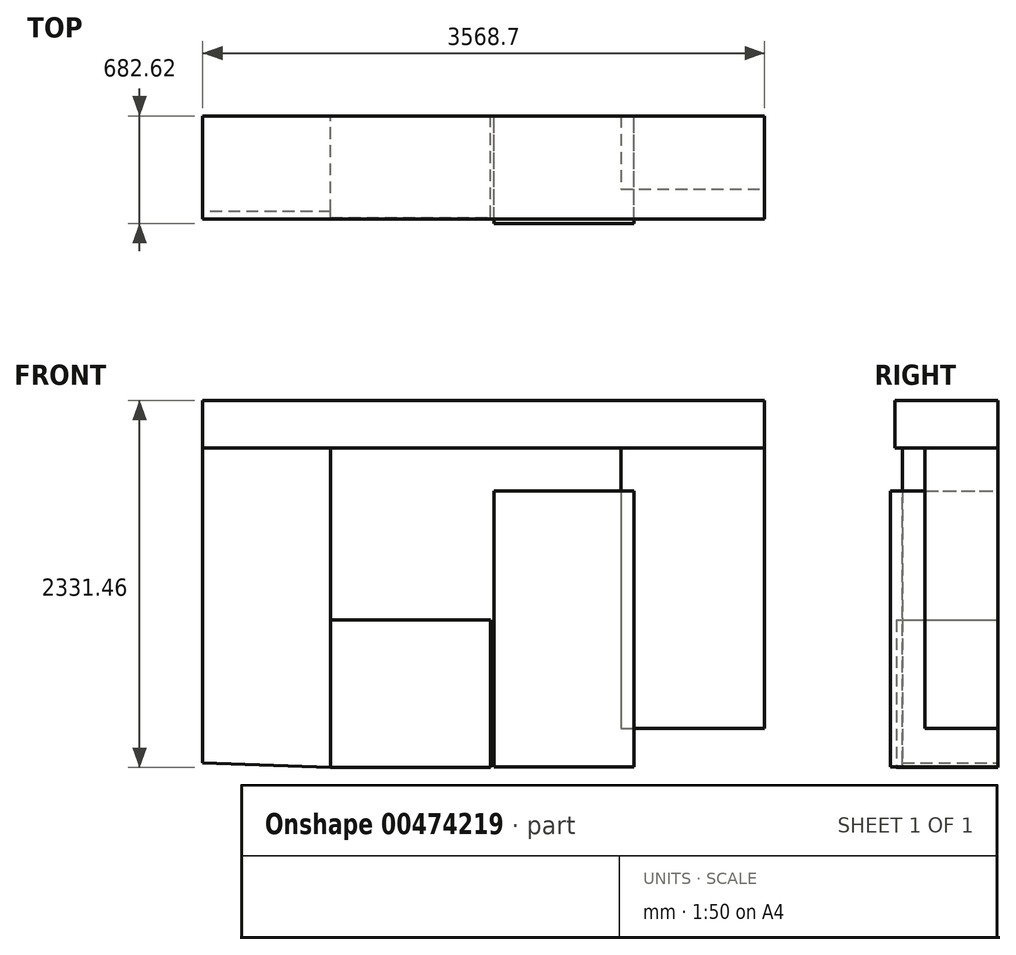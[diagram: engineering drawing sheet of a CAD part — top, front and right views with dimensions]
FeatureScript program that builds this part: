
annotation { "Feature Type Name" : "Feature", "Feature Type Description" : "" }
export const myFeature = defineFeature(function(context is Context, id is Id, definition is map)
    precondition{}
    {
        {
            var Q0;
            Q0=qCreatedBy(makeId("Front.planeOp"),FACE);
            var sketch = newSketch(context, id + "F0", { "sketchPlane" : qUnion([Q0])});
            skLineSegment(sketch, "E0", {"start": v(-765.79, -907.19) * mm, "end": v(-765.79, 1093.06) * mm});
            skLineSegment(sketch, "E1", {"start": v(-765.79, 1093.06) * mm, "end": v(47.01, 1093.06) * mm});
            skLineSegment(sketch, "E2", {"start": v(47.01, 1093.06) * mm, "end": v(47.01, -936.77) * mm});
            skLineSegment(sketch, "E3", {"start": v(47.01, -936.77) * mm, "end": v(-765.79, -907.19) * mm});
            skSolve(sketch);
        }
        {
            var Q0;
            Q0 = qSketchRegion(id + "F0", true);
            extrude(context, id + "F1", {"entities" : qUnion([Q0]), "depth" : 606.42 * mm});
        }
        {
            var Q0;
            Q0=makeQuery(id+"F1.opExtrude","CAP_FACE",FACE,{"disambiguationData":[OSD([sQuery(id+"F0.wireOp",EDGE,"E0"),sQuery(id+"F0.wireOp",EDGE,"E1"),sQuery(id+"F0.wireOp",EDGE,"E2"),sQuery(id+"F0.wireOp",EDGE,"E3")])],"isStart":false});
            var sketch = newSketch(context, id + "F2", { "sketchPlane" : qUnion([Q0])});
            skLineSegment(sketch, "E4", {"start": v(47.01, 0) * mm, "end": v(1063.01, 0) * mm});
            skLineSegment(sketch, "E5", {"start": v(1063.01, 0) * mm, "end": v(1063.01, -936.77) * mm});
            skLineSegment(sketch, "E6", {"start": v(1063.01, -936.77) * mm, "end": v(47.01, -936.77) * mm});
            skLineSegment(sketch, "E7", {"start": v(47.01, -936.77) * mm, "end": v(47.01, 0) * mm});
            skSolve(sketch);
        }
        {
            var Q0;
            Q0 = qSketchRegion(id + "F2", true);
            extrude(context, id + "F3", {"entities" : qUnion([Q0]), "operationType" : NewBodyOperationType.ADD, "depth" : 38.1 * mm, "hasSecondDirection" : true, "secondDirectionOppositeDirection" : true, "secondDirectionDepth" : 606.42 * mm});
        }
        {
            var Q0;
            Q0=makeQuery(id+"F1.opExtrude","CAP_FACE",FACE,{"disambiguationData":[OSD([sQuery(id+"F0.wireOp",EDGE,"E0"),sQuery(id+"F0.wireOp",EDGE,"E1"),sQuery(id+"F0.wireOp",EDGE,"E2"),sQuery(id+"F0.wireOp",EDGE,"E3")])],"isStart":false});
            var sketch = newSketch(context, id + "F4", { "sketchPlane" : qUnion([Q0])});
            skLineSegment(sketch, "E8.bottom", {"start": v(-765.79, 1093.06) * mm, "end": v(2802.91, 1093.06) * mm});
            skLineSegment(sketch, "E8.top", {"start": v(-765.79, 1394.69) * mm, "end": v(2802.91, 1394.69) * mm});
            skLineSegment(sketch, "E8.left", {"start": v(-765.79, 1093.06) * mm, "end": v(-765.79, 1394.69) * mm});
            skLineSegment(sketch, "E8.right", {"start": v(2802.91, 1093.06) * mm, "end": v(2802.91, 1394.69) * mm});
            skSolve(sketch);
        }
        {
            var Q0;
            Q0 = qSketchRegion(id + "F4", true);
            extrude(context, id + "F5", {"entities" : qUnion([Q0]), "operationType" : NewBodyOperationType.ADD, "oppositeDirection" : true, "depth" : 606.42 * mm, "hasSecondDirection" : true, "secondDirectionOppositeDirection" : false, "secondDirectionDepth" : 47.62 * mm});
        }
        {
            var Q0;
            Q0=makeQuery(id+"F1.opExtrude","CAP_FACE",FACE,{"disambiguationData":[OSD([sQuery(id+"F0.wireOp",EDGE,"E0"),sQuery(id+"F0.wireOp",EDGE,"E1"),sQuery(id+"F0.wireOp",EDGE,"E2"),sQuery(id+"F0.wireOp",EDGE,"E3")])],"isStart":false});
            var sketch = newSketch(context, id + "F6", { "sketchPlane" : qUnion([Q0])});
            skLineSegment(sketch, "E9.bottom", {"start": v(1084.55, -933.9) * mm, "end": v(1973.55, -933.9) * mm});
            skLineSegment(sketch, "E9.top", {"start": v(1084.55, 818.7) * mm, "end": v(1973.55, 818.7) * mm});
            skLineSegment(sketch, "E9.left", {"start": v(1084.55, -933.9) * mm, "end": v(1084.55, 818.7) * mm});
            skLineSegment(sketch, "E9.right", {"start": v(1973.55, -933.9) * mm, "end": v(1973.55, 818.7) * mm});
            skSolve(sketch);
        }
        {
            var Q0;
            Q0=makeQuery(id+"F6.imprint","IMPRINT",FACE,{"disambiguationData":[TD([[makeQuery(id+"F6.imprint","IMPRINT",EDGE,{"derivedFrom":sQuery(id+"F6.wireOp",EDGE,"E9.bottom")}),1.0]])]});
            extrude(context, id + "F7", {"entities" : qUnion([Q0]), "depth" : 76.2 * mm, "hasSecondDirection" : true, "secondDirectionOppositeDirection" : true, "secondDirectionDepth" : 606.42 * mm});
        }
        {
            var Q0;
            Q0=makeQuery(id+"F5.opExtrude","SWEPT_FACE",FACE,{"disambiguationData":[OSD([sQuery(id+"F4.wireOp",EDGE,"E8.right")])]});
            var sketch = newSketch(context, id + "F8", { "sketchPlane" : qUnion([Q0])});
            skLineSegment(sketch, "E10.bottom", {"start": v(0, 1093.06) * mm, "end": v(-463.56, 1093.06) * mm});
            skLineSegment(sketch, "E10.top", {"start": v(0, -688.65) * mm, "end": v(-463.56, -688.65) * mm});
            skLineSegment(sketch, "E10.left", {"start": v(0, 1093.06) * mm, "end": v(0, -688.65) * mm});
            skLineSegment(sketch, "E10.right", {"start": v(-463.56, 1093.06) * mm, "end": v(-463.56, -688.65) * mm});
            skSolve(sketch);
        }
        {
            var Q0;
            Q0 = qSketchRegion(id + "F8", true);
            extrude(context, id + "F9", {"entities" : qUnion([Q0]), "oppositeDirection" : true, "depth" : 911.22 * mm});
        }
    });
